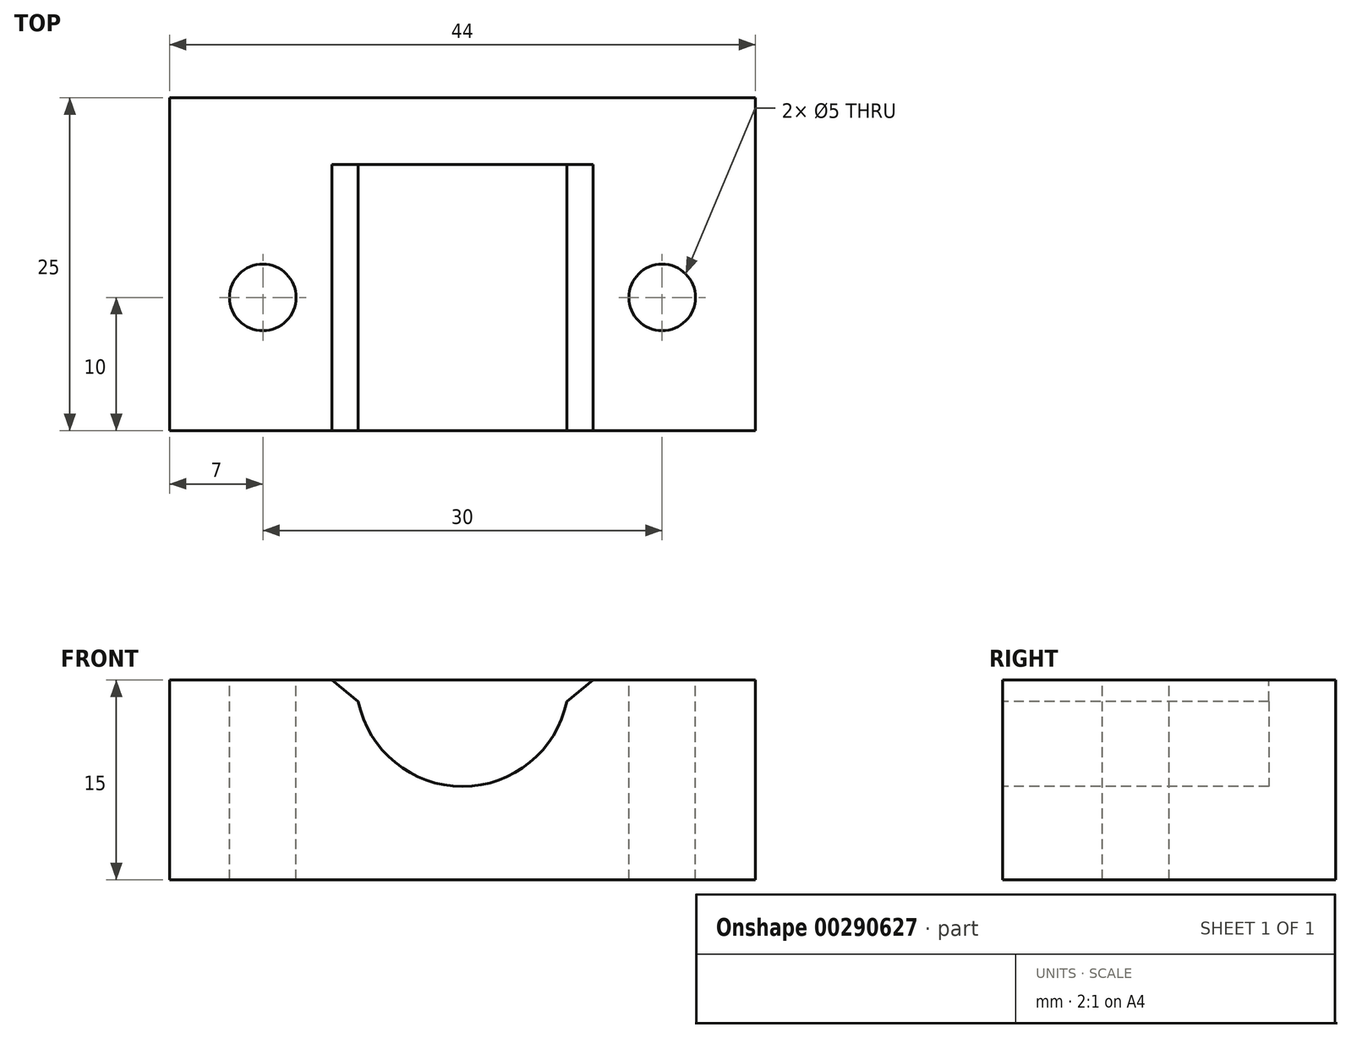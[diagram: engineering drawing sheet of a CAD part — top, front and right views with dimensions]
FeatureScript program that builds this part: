
annotation { "Feature Type Name" : "Feature", "Feature Type Description" : "" }
export const myFeature = defineFeature(function(context is Context, id is Id, definition is map)
    precondition{}
    {
        {
            var Q0;
            Q0=qCreatedBy(makeId("Top.planeOp"),FACE);
            var sketch = newSketch(context, id + "F0", { "sketchPlane" : qUnion([Q0])});
            skLineSegment(sketch, "E0.bottom", {"start": v(-22, 12.5) * mm, "end": v(22, 12.5) * mm});
            skLineSegment(sketch, "E0.top", {"start": v(-22, -12.5) * mm, "end": v(22, -12.5) * mm});
            skLineSegment(sketch, "E0.left", {"start": v(-22, 12.5) * mm, "end": v(-22, -12.5) * mm});
            skLineSegment(sketch, "E0.right", {"start": v(22, 12.5) * mm, "end": v(22, -12.5) * mm});
            skLineSegment(sketch, "E1", {"start": v(0, 12.5) * mm, "end": v(0, -12.5) * mm, "construction": true});
            skSolve(sketch);
        }
        {
            var Q0;
            Q0 = qSketchRegion(id + "F0", true);
            extrude(context, id + "F1", {"entities" : qUnion([Q0]), "depth" : 15 * mm});
        }
        {
            var Q0;
            Q0=makeQuery(id+"F1.opExtrude","SWEPT_FACE",FACE,{"disambiguationData":[OSD([sQuery(id+"F0.wireOp",EDGE,"E0.top")])]});
            var sketch = newSketch(context, id + "F2", { "sketchPlane" : qUnion([Q0])});
            skCircle(sketch, "E2", {"center": v(0, 15) * mm, "radius": 8 * mm});
            skSolve(sketch);
        }
        {
            var Q0;
            Q0 = qSketchRegion(id + "F2", true);
            extrude(context, id + "F3", {"entities" : qUnion([Q0]), "operationType" : NewBodyOperationType.REMOVE, "oppositeDirection" : true, "depth" : 20 * mm});
        }
        {
            var Q0;
            Q0=makeQuery(id+"F1.opExtrude","CAP_FACE",FACE,{"disambiguationData":[OSD([sQuery(id+"F0.wireOp",EDGE,"E0.bottom"),sQuery(id+"F0.wireOp",EDGE,"E0.top"),sQuery(id+"F0.wireOp",EDGE,"E0.left"),sQuery(id+"F0.wireOp",EDGE,"E0.right")])],"isStart":false});
            var sketch = newSketch(context, id + "F4", { "sketchPlane" : qUnion([Q0])});
            skLineSegment(sketch, "E3", {"start": v(-8, 7.5) * mm, "end": v(-22, 7.5) * mm, "construction": true});
            skLineSegment(sketch, "E4", {"start": v(8, 7.5) * mm, "end": v(22, 7.5) * mm, "construction": true});
            skLineSegment(sketch, "E5", {"start": v(-15, 7.5) * mm, "end": v(-15, -12.5) * mm, "construction": true});
            skLineSegment(sketch, "E6", {"start": v(15, 7.5) * mm, "end": v(15, -12.5) * mm, "construction": true});
            skCircle(sketch, "E7", {"center": v(-15, -2.5) * mm, "radius": 2.5 * mm});
            skCircle(sketch, "E8", {"center": v(15, -2.5) * mm, "radius": 2.5 * mm});
            skSolve(sketch);
        }
        {
            var Q0;
            Q0=makeQuery(id+"F4.imprint","IMPRINT",FACE,{"disambiguationData":[TD([[makeQuery(id+"F4.imprint","IMPRINT",EDGE,{"derivedFrom":sQuery(id+"F4.wireOp",EDGE,"E7")}),1.0]])]});
            var Q1;
            Q1=makeQuery(id+"F4.imprint","IMPRINT",FACE,{"disambiguationData":[TD([[makeQuery(id+"F4.imprint","IMPRINT",EDGE,{"derivedFrom":sQuery(id+"F4.wireOp",EDGE,"E8")}),1.0]])]});
            extrude(context, id + "F5", {"entities" : qUnion([Q0, Q1]), "operationType" : NewBodyOperationType.REMOVE, "oppositeDirection" : true, "depth" : 15 * mm});
        }
        {
            var Q0;
            Q0=makeQuery(id+"F3.boolean.opBoolean","INTERSECT",EDGE,{"disambiguationData":[OD(1.0)],"derivedFrom":[makeQuery(id+"F1.opExtrude","CAP_FACE",FACE,{"disambiguationData":[OSD([sQuery(id+"F0.wireOp",EDGE,"E0.bottom"),sQuery(id+"F0.wireOp",EDGE,"E0.top"),sQuery(id+"F0.wireOp",EDGE,"E0.left"),sQuery(id+"F0.wireOp",EDGE,"E0.right")])],"isStart":false}),makeQuery(id+"F3.opExtrude","SWEPT_FACE",FACE,{"disambiguationData":[OSD([sQuery(id+"F2.wireOp",EDGE,"E2")])]})]});
            var Q1;
            Q1=makeQuery(id+"F3.boolean.opBoolean","INTERSECT",EDGE,{"disambiguationData":[OD(0.0)],"derivedFrom":[makeQuery(id+"F1.opExtrude","CAP_FACE",FACE,{"disambiguationData":[OSD([sQuery(id+"F0.wireOp",EDGE,"E0.bottom"),sQuery(id+"F0.wireOp",EDGE,"E0.top"),sQuery(id+"F0.wireOp",EDGE,"E0.left"),sQuery(id+"F0.wireOp",EDGE,"E0.right")])],"isStart":false}),makeQuery(id+"F3.opExtrude","SWEPT_FACE",FACE,{"disambiguationData":[OSD([sQuery(id+"F2.wireOp",EDGE,"E2")])]})]});
            chamfer(context, id + "F6", {"entities" : qUnion([Q0, Q1]), "width" : 2 * mm, "tangentPropagation" : true});
        }
    });
